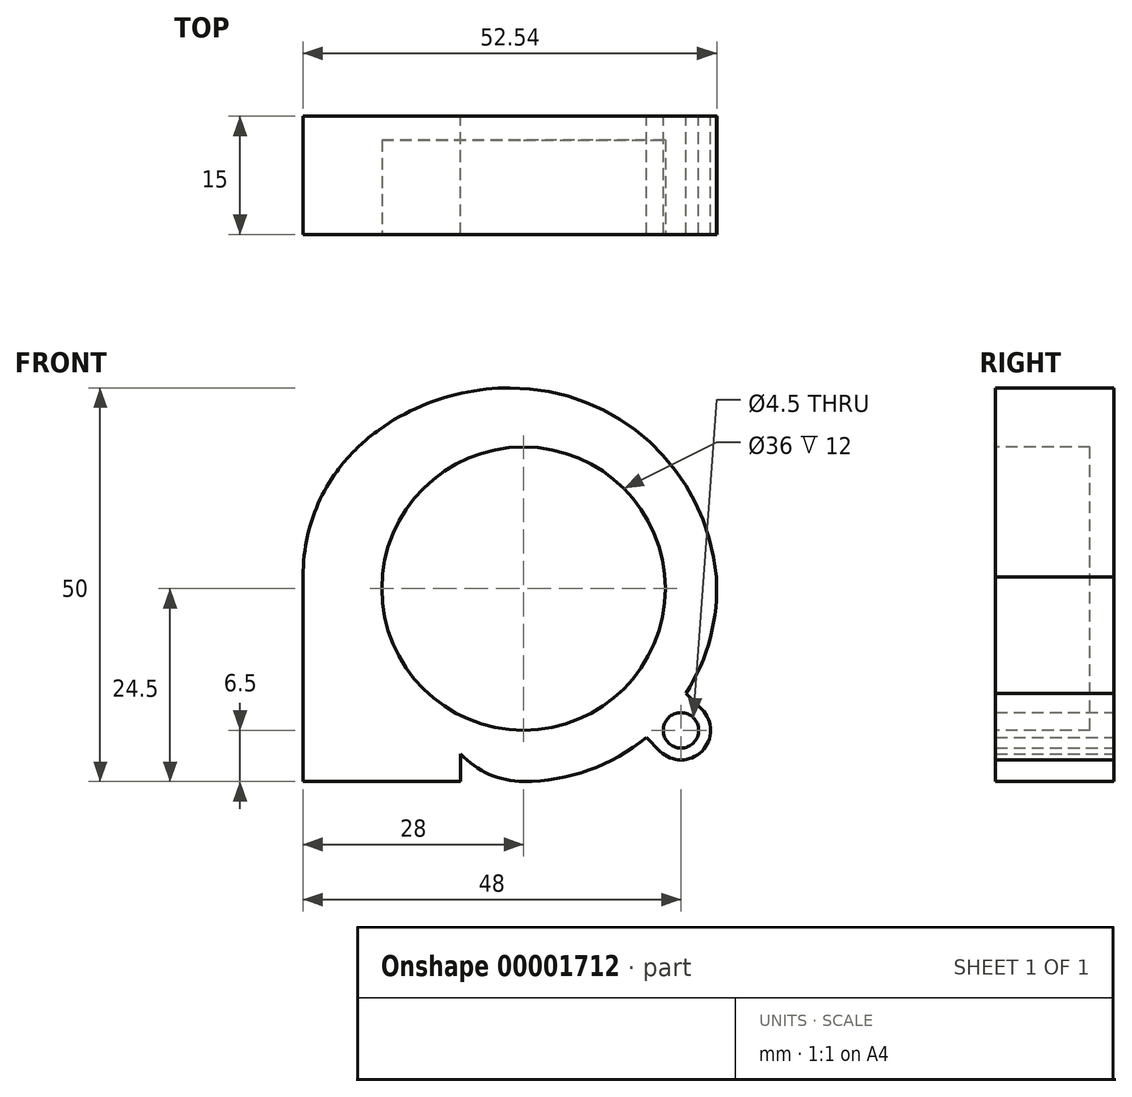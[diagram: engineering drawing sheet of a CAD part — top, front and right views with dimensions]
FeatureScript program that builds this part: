
annotation { "Feature Type Name" : "Feature", "Feature Type Description" : "" }
export const myFeature = defineFeature(function(context is Context, id is Id, definition is map)
    precondition{}
    {
        {
            var Q0;
            Q0=qCreatedBy(makeId("Front.planeOp"),FACE);
            var sketch = newSketch(context, id + "F0", { "sketchPlane" : qUnion([Q0])});
            skLineSegment(sketch, "E0", {"start": v(0, 0) * mm, "end": v(0, 26) * mm});
            skLineSegment(sketch, "E1", {"start": v(26.25, 50) * mm, "end": v(26.25, 26) * mm, "construction": true});
            skLineSegment(sketch, "E2", {"start": v(0, 26) * mm, "end": v(69.48, 26) * mm, "construction": true});
            skLineSegment(sketch, "E3", {"start": v(0, 0) * mm, "end": v(20, 0) * mm});
            skLineSegment(sketch, "E4", {"start": v(20, 0) * mm, "end": v(20, 3.5) * mm});
            skArc(sketch, "E5", {"start": v(52.5, 26) * mm, "mid": v(51.73, 18.29) * mm, "end": v(48.6, 11.2) * mm});
            skArc(sketch, "E6", {"start": v(28, 0) * mm, "mid": v(23.63, 0.91) * mm, "end": v(20, 3.5) * mm});
            skLineSegment(sketch, "E7", {"start": v(28, 24.54) * mm, "end": v(28, -18.24) * mm, "construction": true});
            skFitSpline(sketch, "E8", {"points": [v(0, 26) * mm, v(26.25, 50) * mm], "startDerivative": vector(0, 45.8) * mm, "endDerivative": vector(37.86, 0) * mm});
            skArc(sketch, "E9", {"start": v(26.25, 50) * mm, "mid": v(44.03, 43.1) * mm, "end": v(52.5, 26) * mm});
            skCircle(sketch, "E10", {"center": v(4.5, 44.5) * mm, "radius": 2.25 * mm});
            skLineSegment(sketch, "E11", {"start": v(4.5, 44.5) * mm, "end": v(-16.9, 44.5) * mm, "construction": true});
            skLineSegment(sketch, "E12", {"start": v(0, 26) * mm, "end": v(0, 67.56) * mm});
            skArc(sketch, "E13", {"start": v(7.15, 47.15) * mm, "mid": v(1.85, 47.15) * mm, "end": v(1.85, 41.85) * mm});
            skLineSegment(sketch, "E14", {"start": v(1.85, 41.85) * mm, "end": v(4.29, 39.4) * mm});
            skLineSegment(sketch, "E15", {"start": v(7.15, 47.15) * mm, "end": v(9.63, 44.68) * mm});
            skFitSpline(sketch, "E16.trimOffspring", {"points": [v(0, 26) * mm, v(26.25, 50) * mm], "startDerivative": vector(0, 45.8) * mm, "endDerivative": vector(37.86, 0) * mm});
            skCircle(sketch, "E17", {"center": v(48, 6.5) * mm, "radius": 2.25 * mm});
            skLineSegment(sketch, "E18", {"start": v(48, 6.5) * mm, "end": v(65.35, 6.5) * mm, "construction": true});
            skLineSegment(sketch, "E19", {"start": v(48, 6.5) * mm, "end": v(48, -11.27) * mm, "construction": true});
            skArc(sketch, "E20", {"start": v(45.35, 3.85) * mm, "mid": v(50.65, 3.85) * mm, "end": v(50.65, 9.15) * mm});
            skLineSegment(sketch, "E21", {"start": v(50.65, 9.15) * mm, "end": v(48.6, 11.2) * mm});
            skLineSegment(sketch, "E22", {"start": v(45.35, 3.85) * mm, "end": v(43.6, 5.6) * mm});
            skArc(sketch, "E23.trimOffspring", {"start": v(43.6, 5.6) * mm, "mid": v(36.29, 1.44) * mm, "end": v(28, 0) * mm});
            skSolve(sketch);
        }
        {
            var Q0;
            Q0=makeQuery(id+"F0.imprint","IMPRINT",FACE,{"disambiguationData":[TD([[makeQuery(id+"F0.imprint","IMPRINT",EDGE,{"derivedFrom":sQuery(id+"F0.wireOp",EDGE,"E0")}),-1.0]])]});
            extrude(context, id + "F1", {"entities" : qUnion([Q0]), "depth" : 15 * mm});
        }
        {
            var Q0;
            Q0=makeQuery(id+"F1.opExtrude","CAP_FACE",FACE,{"disambiguationData":[OSD([sQuery(id+"F0.wireOp",EDGE,"E0"),sQuery(id+"F0.wireOp",EDGE,"E3"),sQuery(id+"F0.wireOp",EDGE,"E4"),sQuery(id+"F0.wireOp",EDGE,"E5"),sQuery(id+"F0.wireOp",EDGE,"E6"),sQuery(id+"F0.wireOp",EDGE,"E8"),sQuery(id+"F0.wireOp",EDGE,"E9"),sQuery(id+"F0.wireOp",EDGE,"E10"),sQuery(id+"F0.wireOp",EDGE,"E13"),sQuery(id+"F0.wireOp",EDGE,"E14"),sQuery(id+"F0.wireOp",EDGE,"E15"),sQuery(id+"F0.wireOp",EDGE,"E16.trimOffspring"),sQuery(id+"F0.wireOp",EDGE,"E17"),sQuery(id+"F0.wireOp",EDGE,"E20"),sQuery(id+"F0.wireOp",EDGE,"E21"),sQuery(id+"F0.wireOp",EDGE,"E22"),sQuery(id+"F0.wireOp",EDGE,"E23.trimOffspring")])],"isStart":false});
            var sketch = newSketch(context, id + "F2", { "sketchPlane" : qUnion([Q0])});
            skCircle(sketch, "E24", {"center": v(28, 24.5) * mm, "radius": 18 * mm});
            skLineSegment(sketch, "E25", {"start": v(28, 24.5) * mm, "end": v(-7.83, 24.5) * mm, "construction": true});
            skLineSegment(sketch, "E26", {"start": v(28, 24.5) * mm, "end": v(28, -5.46) * mm, "construction": true});
            skSolve(sketch);
        }
        {
            var Q0;
            Q0=makeQuery(id+"F2.imprint","IMPRINT",FACE,{"disambiguationData":[TD([[makeQuery(id+"F2.imprint","IMPRINT",EDGE,{"derivedFrom":sQuery(id+"F2.wireOp",EDGE,"E24")}),1.0]])]});
            extrude(context, id + "F3", {"entities" : qUnion([Q0]), "operationType" : NewBodyOperationType.REMOVE, "oppositeDirection" : true, "depth" : 12 * mm});
        }
    });
